# Revit family: Valve_Trim-Pressure_Balance-Grohe-Eurosmart_Cosmopolitan-14463000
name_source: partatom
category: Plumbing Fixtures
units: mm (PartAtom-declared; Revit-internal decimal feet)

## family parameters
Cut with Voids When Loaded = No
Host = Face
OmniClass Number = 23.45.05.14.17
OmniClass Title = Showers
Part Type = Normal
Room Calculation Point = No
Round Connector Dimension = Use Diameter
Shared = Yes

## types (1)
- 14463000
    ADA Compliant = Yes
    Assembly Code = D2010710
    CW Connection = No
    CWFU = 3
    Default Elevation = 44"
    Description = Eurosmart Cosmopolitan Pressure Balance Valve Trim with Cartridge
    Finish = Metal-Grohe-000-Starlight Chrome
    Flow Rate = 5.2 gpm (bottom) and 3.0 gpm (top port) at 45 psi (19 L/min)
    HW Connection = No
    HWFU = 3
    Handle Width (2-15/16" to 3-3/4") = 2 15/16"
    Height = 6 13/16"
    Installation Type = Wall Mounted
    Length = 6 5/16"
    Manufacturer = Grohe
    Material = Metal-Grohe-000-Starlight Chrome
    Model = 14463000
    Price = Prices may vary. Please consult Manufacturer Representative for most up-to-date price list.
    Product Documentation Link = https://americanstandard.box.com
    Product Page URL = https://www.grohe.us
    Revised Date = 05/13/2021
    URL = https://www.grohe.us
    Vent Connection = No
    WFU = 4
    Waste Connection = No
    Width = 2 15/16"

## geometry (parser evidence)
native form markers: Sweep x3
no freeform markers — native parametric forms only
